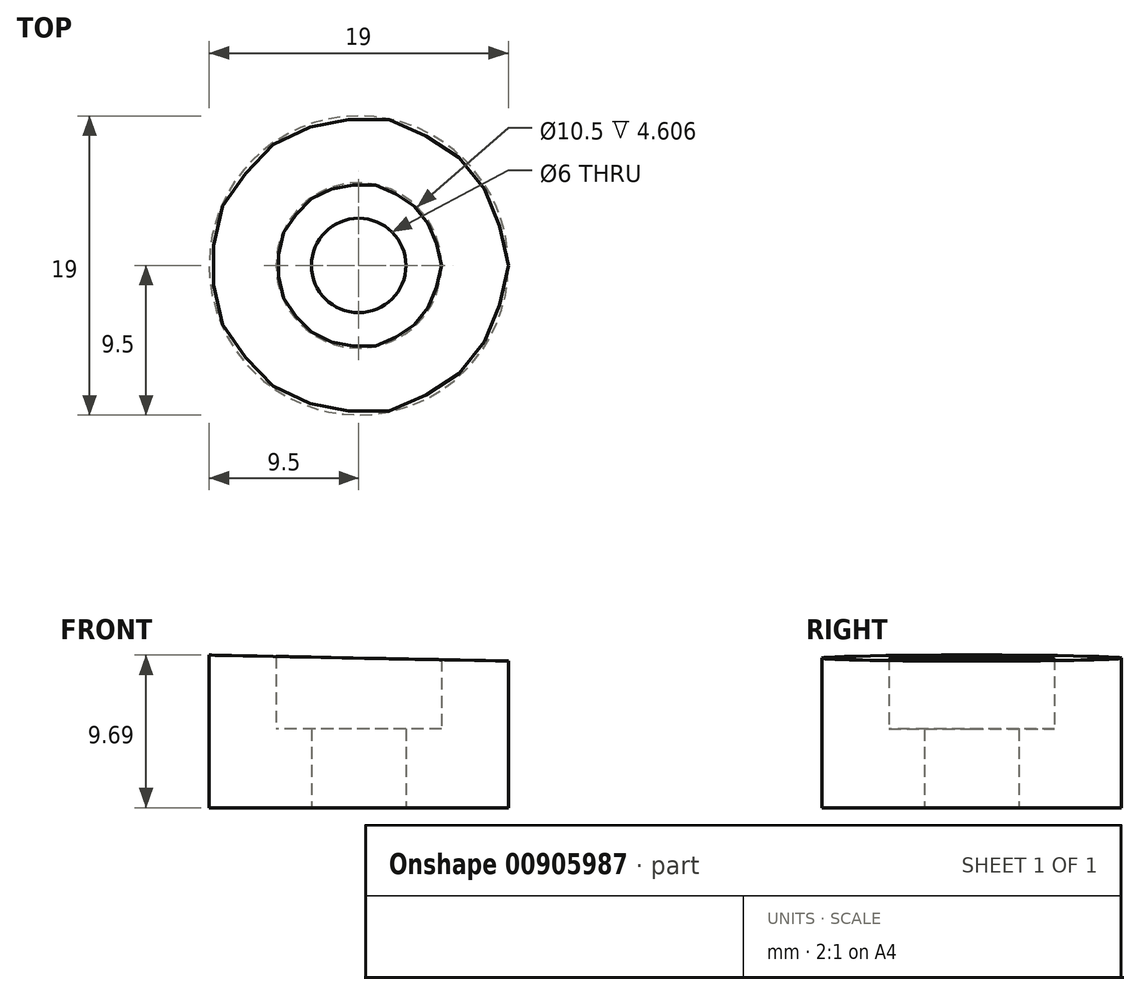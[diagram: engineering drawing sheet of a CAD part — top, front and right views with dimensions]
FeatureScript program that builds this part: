
annotation { "Feature Type Name" : "Feature", "Feature Type Description" : "" }
export const myFeature = defineFeature(function(context is Context, id is Id, definition is map)
    precondition{}
    {
        {
            var Q0;
            Q0=qCreatedBy(makeId("Top.planeOp"),FACE);
            var sketch = newSketch(context, id + "F0", { "sketchPlane" : qUnion([Q0])});
            skCircle(sketch, "E0", {"center": v(0, 0) * mm, "radius": 5.25 * mm});
            skCircle(sketch, "E1", {"center": v(0, 0) * mm, "radius": 9.5 * mm});
            skSolve(sketch);
        }
        {
            var Q0;
            Q0 = qSketchRegion(id + "F0", true);
            extrude(context, id + "F1", {"entities" : qUnion([Q0]), "depth" : 10 * mm, "offsetDistance" : 25 * mm});
        }
        {
            var Q0;
            Q0=qCreatedBy(makeId("Top.planeOp"),FACE);
            var sketch = newSketch(context, id + "F2", { "sketchPlane" : qUnion([Q0])});
            skCircle(sketch, "E2", {"center": v(0, 0) * mm, "radius": 3 * mm});
            skCircle(sketch, "E3.0", {"center": v(0, 0) * mm, "radius": 5.25 * mm});
            skSolve(sketch);
        }
        {
            var Q0;
            Q0 = qSketchRegion(id + "F2", true);
            extrude(context, id + "F3", {"entities" : qUnion([Q0]), "operationType" : NewBodyOperationType.ADD, "depth" : 5 * mm, "offsetDistance" : 25 * mm});
        }
        {
            var Q0;
            Q0=qCreatedBy(makeId("Front.planeOp"),FACE);
            var sketch = newSketch(context, id + "F4", { "sketchPlane" : qUnion([Q0])});
            skLineSegment(sketch, "E4.bottom", {"start": v(-25, 10) * mm, "end": v(25, 9) * mm});
            skLineSegment(sketch, "E4.top", {"start": v(-25, 0) * mm, "end": v(25, 0) * mm});
            skLineSegment(sketch, "E4.left", {"start": v(-25, 10) * mm, "end": v(-25, 0) * mm});
            skLineSegment(sketch, "E4.right", {"start": v(25, 9) * mm, "end": v(25, 0) * mm});
            skPoint(sketch, "E5", {"position": v(0, 9.5) * mm});
            skLineSegment(sketch, "E6.0", {"start": v(-9.5, 10) * mm, "end": v(9.5, 10) * mm});
            skSolve(sketch);
        }
        {
            var Q0;
            Q0 = qSketchRegion(id + "F4", true);
            extrude(context, id + "F5", {"entities" : qUnion([Q0]), "operationType" : NewBodyOperationType.INTERSECT, "endBound" : BoundingType.SYMMETRIC, "oppositeDirection" : true, "depth" : 25 * mm, "offsetDistance" : 25 * mm});
        }
    });
